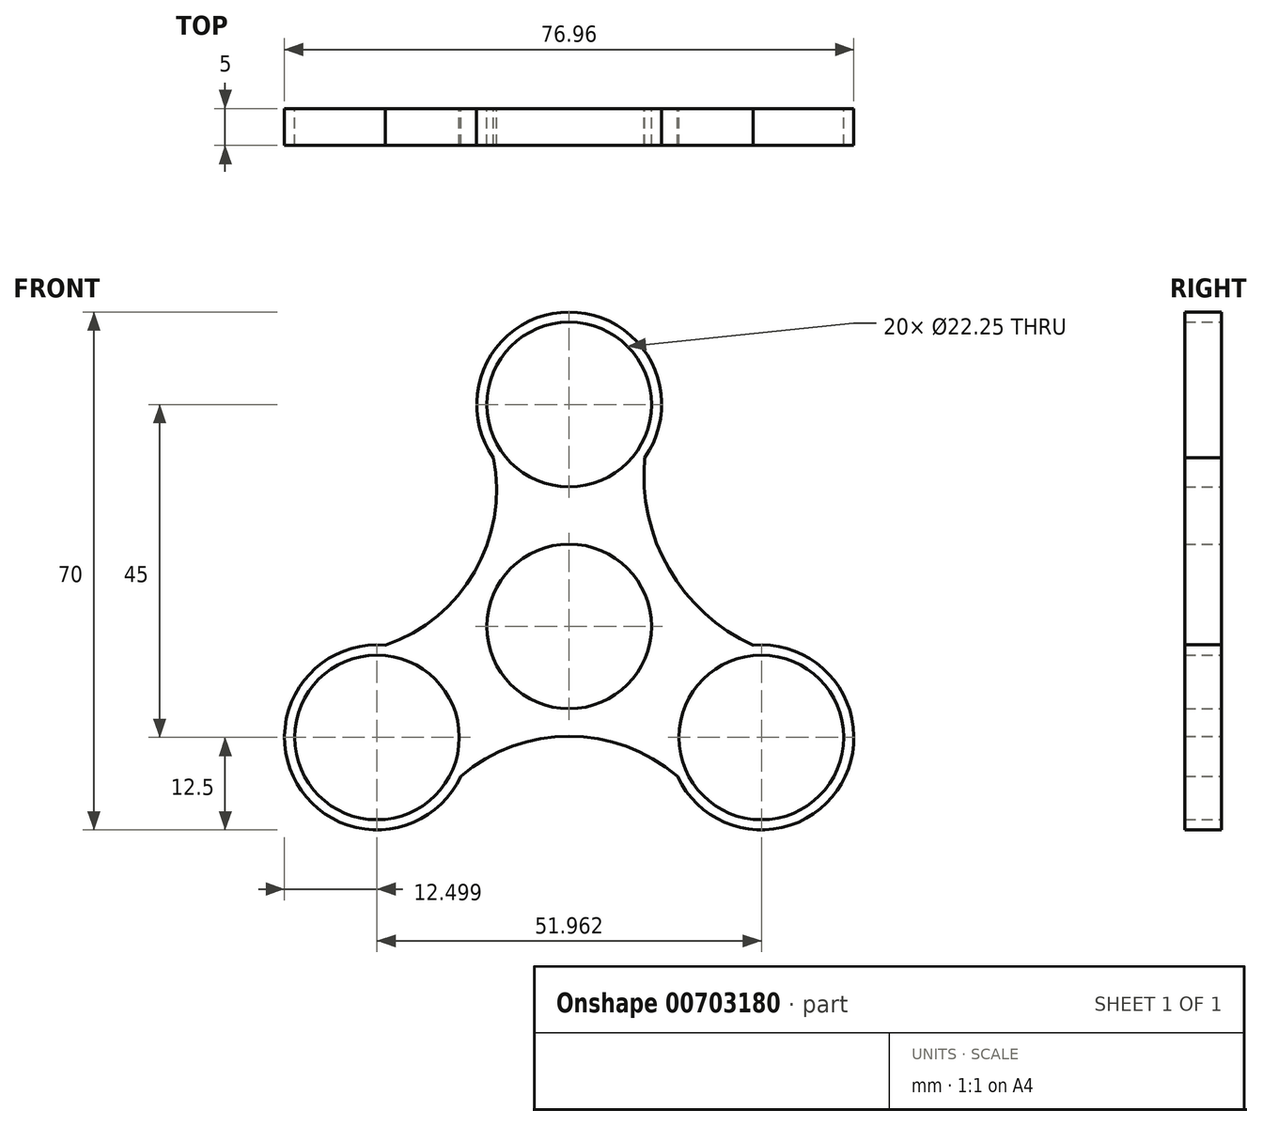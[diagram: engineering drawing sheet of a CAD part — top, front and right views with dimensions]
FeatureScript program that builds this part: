
annotation { "Feature Type Name" : "Feature", "Feature Type Description" : "" }
export const myFeature = defineFeature(function(context is Context, id is Id, definition is map)
    precondition{}
    {
        {
            var Q0;
            Q0=qCreatedBy(makeId("Front.planeOp"),FACE);
            var sketch = newSketch(context, id + "F0", { "sketchPlane" : qUnion([Q0])});
            skCircle(sketch, "E0", {"center": v(0, 0) * mm, "radius": 11.12 * mm});
            skCircle(sketch, "E1", {"center": v(0, 30) * mm, "radius": 11.12 * mm});
            skCircle(sketch, "E2.1.1", {"center": v(-25.98, -15) * mm, "radius": 11.12 * mm});
            skCircle(sketch, "E2.2.1", {"center": v(25.98, -15) * mm, "radius": 11.12 * mm});
            skArc(sketch, "E3", {"start": v(10.23, 22.81) * mm, "mid": v(0, 42.5) * mm, "end": v(-10.23, 22.81) * mm});
            skArc(sketch, "E4", {"start": v(14.64, -20.26) * mm, "mid": v(36.8, -21.25) * mm, "end": v(24.87, -2.55) * mm});
            skArc(sketch, "E5", {"start": v(-24.87, -2.55) * mm, "mid": v(-36.8, -21.25) * mm, "end": v(-14.64, -20.26) * mm});
            skArc(sketch, "E6", {"start": v(-24.87, -2.55) * mm, "mid": v(-12.79, 7.38) * mm, "end": v(-10.23, 22.81) * mm});
            skArc(sketch, "E7", {"start": v(10.23, 22.81) * mm, "mid": v(13.48, 7.78) * mm, "end": v(24.87, -2.55) * mm});
            skArc(sketch, "E8", {"start": v(14.64, -20.26) * mm, "mid": v(0, -14.85) * mm, "end": v(-14.64, -20.26) * mm});
            skSolve(sketch);
        }
        {
            var Q0;
            Q0 = qSketchRegion(id + "F0", true);
            extrude(context, id + "F1", {"entities" : qUnion([Q0]), "depth" : 5 * mm, "offsetDistance" : 25 * mm});
        }
    });
